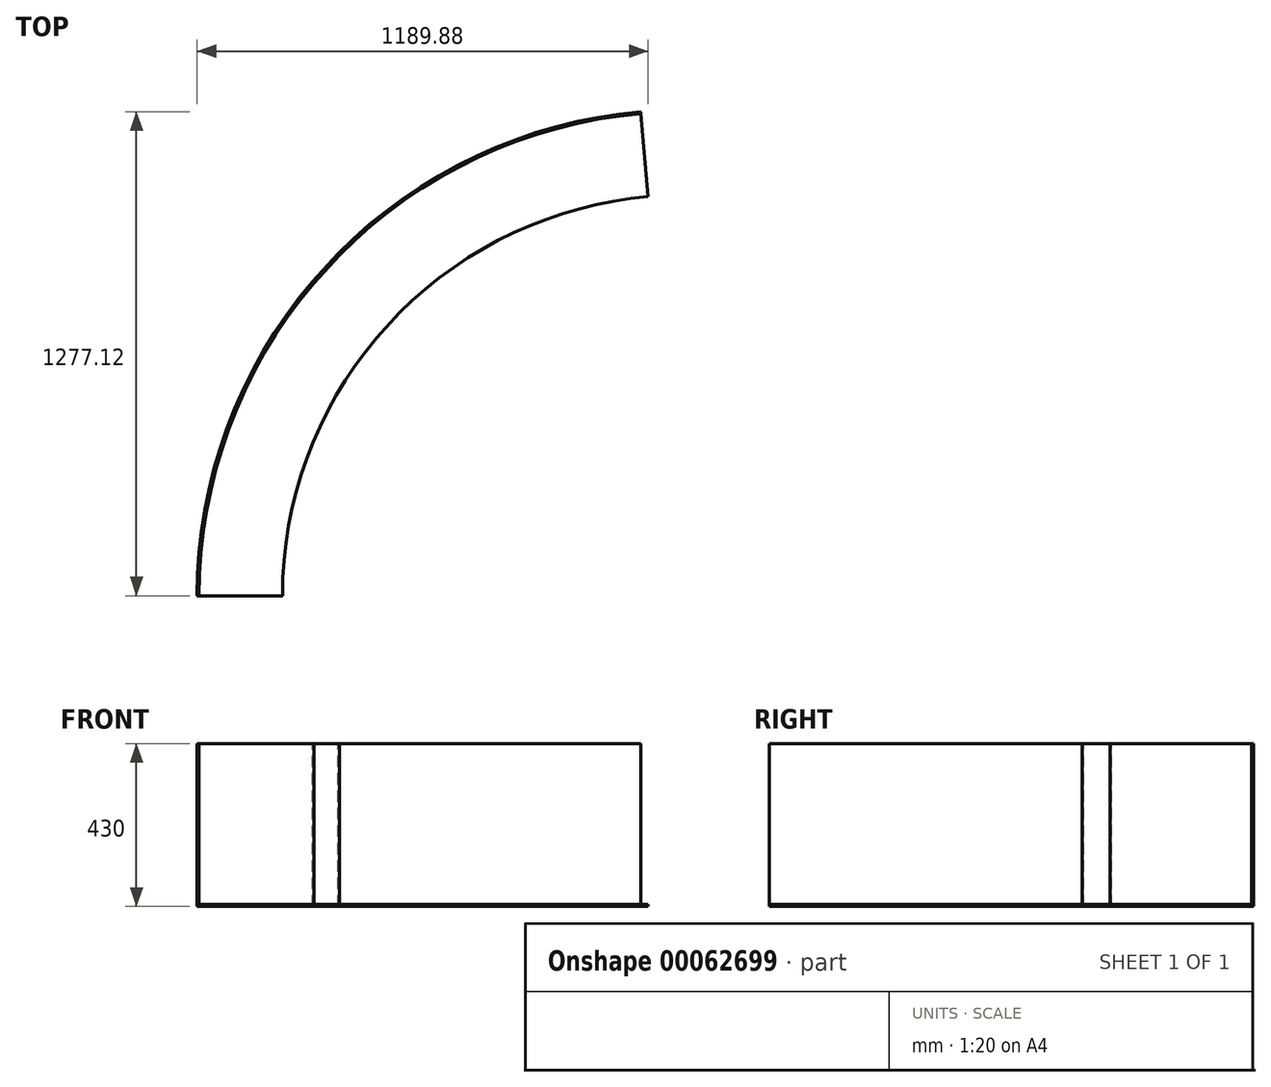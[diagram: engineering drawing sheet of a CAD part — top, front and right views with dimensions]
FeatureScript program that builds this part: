
annotation { "Feature Type Name" : "Feature", "Feature Type Description" : "" }
export const myFeature = defineFeature(function(context is Context, id is Id, definition is map)
    precondition{}
    {
        {
            var Q0;
            Q0=qCreatedBy(makeId("Front.planeOp"),FACE);
            var sketch = newSketch(context, id + "F0", { "sketchPlane" : qUnion([Q0])});
            skLineSegment(sketch, "E0", {"start": v(0, 0) * mm, "end": v(-225, 0) * mm});
            skLineSegment(sketch, "E1", {"start": v(-225, 0) * mm, "end": v(-225, 430) * mm});
            skLineSegment(sketch, "E2.0", {"start": v(-220, 5) * mm, "end": v(-220, 430) * mm});
            skLineSegment(sketch, "E2.1", {"start": v(0, 5) * mm, "end": v(-220, 5) * mm});
            skLineSegment(sketch, "E3", {"start": v(-225, 430) * mm, "end": v(-220, 430) * mm});
            skLineSegment(sketch, "E4", {"start": v(0, 5) * mm, "end": v(0, 0) * mm});
            skSolve(sketch);
        }
        {
            var Q0;
            Q0=qCreatedBy(makeId("Top.planeOp"),FACE);
            var sketch = newSketch(context, id + "F1", { "sketchPlane" : qUnion([Q0])});
            skArc(sketch, "E5", {"start": v(945.27, 1277.12) * mm, "mid": v(512.52, 1160.63) * mm, "end": v(146.3, 902.31) * mm});
            skLineSegment(sketch, "E6", {"start": v(1057, 0) * mm, "end": v(78.75, 828.58) * mm, "construction": true});
            skLineSegment(sketch, "E7", {"start": v(1057, 0) * mm, "end": v(146.3, 902.31) * mm, "construction": true});
            skLineSegment(sketch, "E8", {"start": v(78.75, 828.58) * mm, "end": v(146.3, 902.31) * mm});
            skLineSegment(sketch, "E9", {"start": v(1057, 0) * mm, "end": v(112.53, 865.45) * mm, "construction": true});
            skArc(sketch, "E10.trimOffspring", {"start": v(78.75, 828.58) * mm, "mid": v(-146.67, 441.25) * mm, "end": v(-225, 0) * mm});
            skLineSegment(sketch, "E11", {"start": v(1057, 0) * mm, "end": v(945.27, 1277.12) * mm, "construction": true});
            skLineSegment(sketch, "E12", {"start": v(1057, 0) * mm, "end": v(-225, 0) * mm, "construction": true});
            skSolve(sketch);
        }
        {
            var Q0;
            Q0=qSketchRegion(id+"F0",true);
            var Q1;
            Q1=sQuery(id+"F1.wireOp",EDGE,"E5");
            var Q2;
            Q2=sQuery(id+"F1.wireOp",EDGE,"E8");
            var Q3;
            Q3=sQuery(id+"F1.wireOp",EDGE,"E10.trimOffspring");
            sweep(context, id + "F2", {"profiles" : qUnion([Q0]), "path" : qUnion([Q1, Q2, Q3])});
        }
    });
